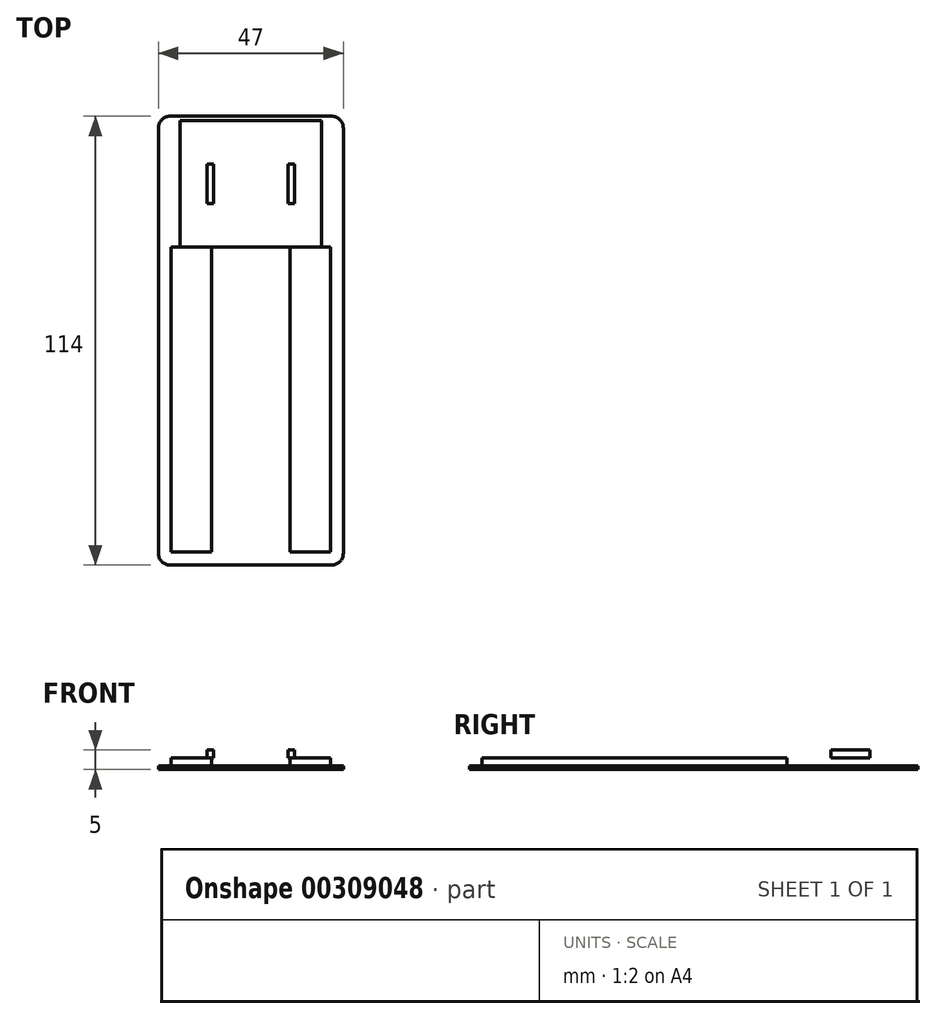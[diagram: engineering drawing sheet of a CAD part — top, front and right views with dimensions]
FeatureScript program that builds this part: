
annotation { "Feature Type Name" : "Feature", "Feature Type Description" : "" }
export const myFeature = defineFeature(function(context is Context, id is Id, definition is map)
    precondition{}
    {
        {
            var Q0;
            Q0=qCreatedBy(makeId("Top.planeOp"),FACE);
            var sketch = newSketch(context, id + "F0", { "sketchPlane" : qUnion([Q0])});
            skLineSegment(sketch, "E0.bottom", {"start": v(-23.5, 57) * mm, "end": v(23.5, 57) * mm});
            skLineSegment(sketch, "E0.top", {"start": v(-23.5, -57) * mm, "end": v(23.5, -57) * mm});
            skLineSegment(sketch, "E0.left", {"start": v(-23.5, 57) * mm, "end": v(-23.5, -57) * mm});
            skLineSegment(sketch, "E0.right", {"start": v(23.5, 57) * mm, "end": v(23.5, -57) * mm});
            skPoint(sketch, "E0.middle", {"position": v(0, 0) * mm});
            skLineSegment(sketch, "E1.bottom", {"start": v(20.25, 23.75) * mm, "end": v(-20.25, 23.75) * mm});
            skLineSegment(sketch, "E1.top", {"start": v(20.25, -53.75) * mm, "end": v(-20.25, -53.75) * mm});
            skLineSegment(sketch, "E1.left", {"start": v(20.25, 23.75) * mm, "end": v(20.25, -53.75) * mm});
            skLineSegment(sketch, "E1.right", {"start": v(-20.25, 23.75) * mm, "end": v(-20.25, -53.75) * mm});
            skPoint(sketch, "E1.middle", {"position": v(0, -15) * mm});
            skLineSegment(sketch, "E2.bottom", {"start": v(18, 23.75) * mm, "end": v(-18, 23.75) * mm});
            skLineSegment(sketch, "E2.top", {"start": v(18, 55.9) * mm, "end": v(-18, 55.9) * mm});
            skLineSegment(sketch, "E2.left", {"start": v(18, 23.75) * mm, "end": v(18, 55.9) * mm});
            skLineSegment(sketch, "E2.right", {"start": v(-18, 23.75) * mm, "end": v(-18, 55.9) * mm});
            skPoint(sketch, "E2.middle", {"position": v(0, 39.83) * mm});
            skSolve(sketch);
        }
        {
            var Q0;
            Q0=makeQuery(id+"F0.imprint","IMPRINT",FACE,{"disambiguationData":[TD([[makeQuery(id+"F0.imprint","IMPRINT",EDGE,{"derivedFrom":sQuery(id+"F0.wireOp",EDGE,"E0.bottom")}),-1.0]])]});
            extrude(context, id + "F1", {"entities" : qUnion([Q0]), "depth" : 1 * mm});
        }
        {
            var Q0;
            Q0=makeQuery(id+"F0.imprint","IMPRINT",FACE,{"disambiguationData":[TD([[makeQuery(id+"F0.imprint","IMPRINT",EDGE,{"derivedFrom":sQuery(id+"F0.wireOp",EDGE,"E1.top")}),-1.0]])]});
            var Q1;
            Q1=makeQuery(id+"F0.imprint","IMPRINT",FACE,{"disambiguationData":[TD([[makeQuery(id+"F0.imprint","IMPRINT",EDGE,{"derivedFrom":sQuery(id+"F0.wireOp",EDGE,"E2.bottom")}),-1.0]])]});
            extrude(context, id + "F2", {"entities" : qUnion([Q0, Q1]), "operationType" : NewBodyOperationType.ADD, "depth" : 3 * mm});
        }
        {
            var Q0;
            Q0=makeQuery(id+"F1.opExtrude","SWEPT_EDGE",EDGE,{"disambiguationData":[OSD([sQuery(id+"F0.wireOp",EDGE,"E0.top"),sQuery(id+"F0.wireOp",EDGE,"E0.right")])]});
            var Q1;
            Q1=makeQuery(id+"F1.opExtrude","SWEPT_EDGE",EDGE,{"disambiguationData":[OSD([sQuery(id+"F0.wireOp",EDGE,"E0.top"),sQuery(id+"F0.wireOp",EDGE,"E0.left")])]});
            var Q2;
            Q2=makeQuery(id+"F1.opExtrude","SWEPT_EDGE",EDGE,{"disambiguationData":[OSD([sQuery(id+"F0.wireOp",EDGE,"E0.bottom"),sQuery(id+"F0.wireOp",EDGE,"E0.right")])]});
            var Q3;
            Q3=makeQuery(id+"F1.opExtrude","SWEPT_EDGE",EDGE,{"disambiguationData":[OSD([sQuery(id+"F0.wireOp",EDGE,"E0.bottom"),sQuery(id+"F0.wireOp",EDGE,"E0.left")])]});
            fillet(context, id + "F3", {"entities" : qUnion([Q0, Q1, Q2, Q3]), "radius" : 3 * mm, "tangentPropagation" : true, "allowEdgeOverflow" : false});
        }
        {
            var Q0;
            Q0=makeQuery(id+"F2.opExtrude","CAP_FACE",FACE,{"disambiguationData":[OSD([sQuery(id+"F0.wireOp",EDGE,"E1.bottom"),sQuery(id+"F0.wireOp",EDGE,"E1.top"),sQuery(id+"F0.wireOp",EDGE,"E1.left"),sQuery(id+"F0.wireOp",EDGE,"E1.right"),sQuery(id+"F0.wireOp",EDGE,"E2.top"),sQuery(id+"F0.wireOp",EDGE,"E2.left"),sQuery(id+"F0.wireOp",EDGE,"E2.right")])],"isStart":false});
            var sketch = newSketch(context, id + "F4", { "sketchPlane" : qUnion([Q0])});
            skLineSegment(sketch, "E3.bottom", {"start": v(10, -53.75) * mm, "end": v(-10, -53.75) * mm});
            skLineSegment(sketch, "E3.top", {"start": v(10, 23.75) * mm, "end": v(-10, 23.75) * mm});
            skLineSegment(sketch, "E3.left", {"start": v(10, -53.75) * mm, "end": v(10, 23.75) * mm});
            skLineSegment(sketch, "E3.right", {"start": v(-10, -53.75) * mm, "end": v(-10, 23.75) * mm});
            skPoint(sketch, "E3.middle", {"position": v(0, -15) * mm});
            skLineSegment(sketch, "E4.bottom", {"start": v(4, 23.75) * mm, "end": v(-4, 23.75) * mm});
            skLineSegment(sketch, "E4.top", {"start": v(4, 55.9) * mm, "end": v(-4, 55.9) * mm});
            skLineSegment(sketch, "E4.left", {"start": v(4, 23.75) * mm, "end": v(4, 55.9) * mm});
            skLineSegment(sketch, "E4.right", {"start": v(-4, 23.75) * mm, "end": v(-4, 55.9) * mm});
            skPoint(sketch, "E4.middle", {"position": v(0, 39.83) * mm});
            skLineSegment(sketch, "E5.bottom", {"start": v(-9.5, 34.82) * mm, "end": v(-11.1, 34.82) * mm});
            skLineSegment(sketch, "E5.top", {"start": v(-9.5, 44.82) * mm, "end": v(-11.1, 44.82) * mm});
            skLineSegment(sketch, "E5.left", {"start": v(-9.5, 34.82) * mm, "end": v(-9.5, 44.82) * mm});
            skLineSegment(sketch, "E5.right", {"start": v(-11.1, 34.82) * mm, "end": v(-11.1, 44.82) * mm});
            skPoint(sketch, "E5.middle", {"position": v(-10.3, 39.83) * mm});
            skLineSegment(sketch, "E6.bottom", {"start": v(11.1, 34.82) * mm, "end": v(9.5, 34.82) * mm});
            skLineSegment(sketch, "E6.top", {"start": v(11.1, 44.82) * mm, "end": v(9.5, 44.82) * mm});
            skLineSegment(sketch, "E6.left", {"start": v(11.1, 34.82) * mm, "end": v(11.1, 44.82) * mm});
            skLineSegment(sketch, "E6.right", {"start": v(9.5, 34.82) * mm, "end": v(9.5, 44.82) * mm});
            skPoint(sketch, "E6.middle", {"position": v(10.3, 39.83) * mm});
            skSolve(sketch);
        }
        {
            var Q0;
            Q0=makeQuery(id+"F4.imprint","IMPRINT",FACE,{"disambiguationData":[TD([[makeQuery(id+"F4.imprint","IMPRINT",EDGE,{"derivedFrom":sQuery(id+"F4.wireOp",EDGE,"E3.bottom")}),-1.0]])]});
            var Q1;
            Q1=makeQuery(id+"F4.imprint","IMPRINT",FACE,{"disambiguationData":[TD([[makeQuery(id+"F4.imprint","IMPRINT",EDGE,{"derivedFrom":sQuery(id+"F4.wireOp",EDGE,"E4.bottom")}),-1.0]])]});
            extrude(context, id + "F5", {"entities" : qUnion([Q0, Q1]), "operationType" : NewBodyOperationType.REMOVE, "oppositeDirection" : true, "depth" : 2 * mm});
        }
        {
            var Q0;
            Q0=makeQuery(id+"F4.imprint","IMPRINT",FACE,{"disambiguationData":[TD([[makeQuery(id+"F4.imprint","IMPRINT",EDGE,{"derivedFrom":sQuery(id+"F4.wireOp",EDGE,"E5.bottom")}),-1.0]])]});
            var Q1;
            Q1=makeQuery(id+"F4.imprint","IMPRINT",FACE,{"disambiguationData":[TD([[makeQuery(id+"F4.imprint","IMPRINT",EDGE,{"derivedFrom":sQuery(id+"F4.wireOp",EDGE,"E6.bottom")}),-1.0]])]});
            extrude(context, id + "F6", {"entities" : qUnion([Q0, Q1]), "operationType" : NewBodyOperationType.ADD, "depth" : 2 * mm});
        }
    });
